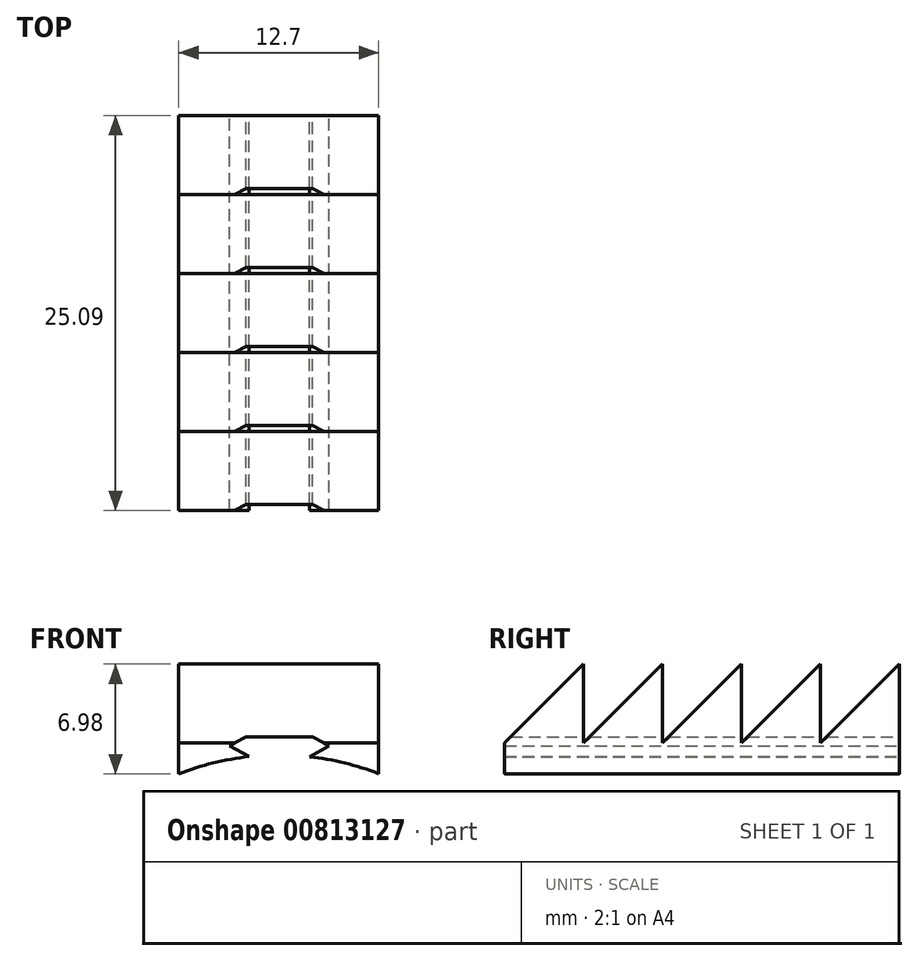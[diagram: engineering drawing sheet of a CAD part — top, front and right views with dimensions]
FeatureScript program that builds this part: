
annotation { "Feature Type Name" : "Feature", "Feature Type Description" : "" }
export const myFeature = defineFeature(function(context is Context, id is Id, definition is map)
    precondition{}
    {
        {
            var Q0;
            Q0=qCreatedBy(makeId("Right.planeOp"),FACE);
            var sketch = newSketch(context, id + "F0", { "sketchPlane" : qUnion([Q0])});
            skLineSegment(sketch, "E0", {"start": v(-27.03, 25.32) * mm, "end": v(-27.03, 20.3) * mm});
            skLineSegment(sketch, "E1", {"start": v(-27.03, 20.3) * mm, "end": v(-22.02, 25.32) * mm});
            skLineSegment(sketch, "E2", {"start": v(-22.02, 25.32) * mm, "end": v(-22.02, 20.3) * mm});
            skLineSegment(sketch, "E3", {"start": v(-27.03, 25.32) * mm, "end": v(-32.05, 20.3) * mm});
            skPoint(sketch, "E4.start.orphan", {"position": v(-5.28, 10.5) * mm});
            skPoint(sketch, "E5.start.orphan", {"position": v(-1.95, 20.3) * mm});
            skPoint(sketch, "E6.orphan", {"position": v(-0.63, 28.3) * mm});
            skPoint(sketch, "E7.right.end.orphan", {"position": v(0, 12.3) * mm});
            skPoint(sketch, "E8.orphan", {"position": v(-0.31, 20.3) * mm});
            skPoint(sketch, "E9.orphan", {"position": v(2.77, 47.92) * mm});
            skPoint(sketch, "E10.orphan", {"position": v(-9.93, -7.31) * mm});
            skPoint(sketch, "E11.orphan", {"position": v(-3.58, 20.3) * mm});
            skLineSegment(sketch, "E12", {"start": v(-22.02, 20.3) * mm, "end": v(-17, 25.32) * mm});
            skLineSegment(sketch, "E13", {"start": v(-17, 25.32) * mm, "end": v(-17, 20.3) * mm});
            skLineSegment(sketch, "E14", {"start": v(-17, 20.3) * mm, "end": v(-17, 25.32) * mm});
            skPoint(sketch, "E14.endSnap0", {"position": v(-17, 20.3) * mm});
            skLineSegment(sketch, "E15", {"start": v(-11.98, 25.32) * mm, "end": v(-17, 20.3) * mm});
            skLineSegment(sketch, "E16", {"start": v(-11.98, 20.3) * mm, "end": v(-11.98, 25.32) * mm});
            skLineSegment(sketch, "E17", {"start": v(-11.98, 20.3) * mm, "end": v(-6.96, 25.32) * mm});
            skLineSegment(sketch, "E18", {"start": v(-6.96, 25.32) * mm, "end": v(-6.96, 20.3) * mm});
            skPoint(sketch, "E19.1.0.0", {"position": v(20.12, 10.5) * mm});
            skPoint(sketch, "E19.2.0.0", {"position": v(45.52, 10.5) * mm});
            skLineSegment(sketch, "E19.direction1", {"start": v(-5.28, 10.5) * mm, "end": v(20.12, 10.5) * mm, "construction": true});
            skLineSegment(sketch, "E20.top", {"start": v(-6.96, 16.73) * mm, "end": v(-32.05, 16.73) * mm});
            skLineSegment(sketch, "E20.left", {"start": v(-6.96, 20.3) * mm, "end": v(-6.96, 16.73) * mm});
            skLineSegment(sketch, "E21", {"start": v(-32.05, 16.73) * mm, "end": v(-32.05, 20.3) * mm});
            skPoint(sketch, "E22.orphan", {"position": v(-31.96, 16.73) * mm});
            skSolve(sketch);
        }
        {
            var Q0;
            Q0=makeQuery(id+"F0.imprint","IMPRINT",FACE,{"disambiguationData":[TD([[makeQuery(id+"F0.imprint","IMPRINT",EDGE,{"derivedFrom":sQuery(id+"F0.wireOp",EDGE,"E0")}),-1.0]])]});
            extrude(context, id + "F1", {"entities" : qUnion([Q0]), "depth" : 12.7 * mm, "offsetDistance" : 25.4 * mm});
        }
        {
            var Q0;
            Q0=makeQuery(id+"F1.opExtrude","CAP_VERTEX",VERTEX,{"disambiguationData":[OSD([sQuery(id+"F0.wireOp",EDGE,"E17"),sQuery(id+"F0.wireOp",EDGE,"E18")])],"isStart":false});
            var Q1;
            Q1=qCreatedBy(makeId("Front.planeOp"),FACE);
            cPlane(context, id + "F2", {"entities" : qUnion([Q0, Q1]), "cplaneType" : CPlaneType.PLANE_POINT, "offset" : 25.4 * mm, "width" : 152.4 * mm, "height" : 152.4 * mm});
        }
        {
            var Q0;
            Q0=qCreatedBy(id+"F2.planeOp",FACE);
            var sketch = newSketch(context, id + "F3", { "sketchPlane" : qUnion([Q0])});
            skCircle(sketch, "E23", {"center": v(6.37, 2.08) * mm, "radius": 17.46 * mm});
            skSolve(sketch);
        }
        {
            var Q0;
            Q0 = qSketchRegion(id + "F3", true);
            extrude(context, id + "F4", {"entities" : qUnion([Q0]), "operationType" : NewBodyOperationType.REMOVE, "depth" : 25.4 * mm, "offsetDistance" : 25.4 * mm});
        }
        {
            var Q0;
            Q0=makeQuery(id+"F1.opExtrude","SWEPT_BODY",BODY,{"disambiguationData":[OSD([sQuery(id+"F0.wireOp",EDGE,"E0"),sQuery(id+"F0.wireOp",EDGE,"E1"),sQuery(id+"F0.wireOp",EDGE,"E2"),sQuery(id+"F0.wireOp",EDGE,"E3"),sQuery(id+"F0.wireOp",EDGE,"E12"),sQuery(id+"F0.wireOp",EDGE,"E13"),sQuery(id+"F0.wireOp",EDGE,"E15"),sQuery(id+"F0.wireOp",EDGE,"E16"),sQuery(id+"F0.wireOp",EDGE,"E17"),sQuery(id+"F0.wireOp",EDGE,"E18"),sQuery(id+"F0.wireOp",EDGE,"E20.top"),sQuery(id+"F0.wireOp",EDGE,"E20.left"),sQuery(id+"F0.wireOp",EDGE,"E20.right"),sQuery(id+"F0.wireOp",EDGE,"0172e36d-b3d0-40e5-9f1f-b767e8603321.trimOffspring")])]});
            transform(context, id + "F5", {"entities" : qUnion([Q0]), "transformType" : TransformType.COPY});
        }
        {
            var Q0;
            Q0=makeQuery(id+"F1.opExtrude","SWEPT_BODY",BODY,{"disambiguationData":[OSD([sQuery(id+"F0.wireOp",EDGE,"E0"),sQuery(id+"F0.wireOp",EDGE,"E1"),sQuery(id+"F0.wireOp",EDGE,"E2"),sQuery(id+"F0.wireOp",EDGE,"E3"),sQuery(id+"F0.wireOp",EDGE,"E12"),sQuery(id+"F0.wireOp",EDGE,"E13"),sQuery(id+"F0.wireOp",EDGE,"E15"),sQuery(id+"F0.wireOp",EDGE,"E16"),sQuery(id+"F0.wireOp",EDGE,"E17"),sQuery(id+"F0.wireOp",EDGE,"E18"),sQuery(id+"F0.wireOp",EDGE,"E20.top"),sQuery(id+"F0.wireOp",EDGE,"E20.left"),sQuery(id+"F0.wireOp",EDGE,"E20.right"),sQuery(id+"F0.wireOp",EDGE,"0172e36d-b3d0-40e5-9f1f-b767e8603321.trimOffspring")])]});
            transform(context, id + "F6", {"entities" : qUnion([Q0]), "transformType" : TransformType.TRANSLATION_3D, "dx" : 0 * mm, "dy" : 26.14 * mm, "dz" : 0 * mm, "makeCopy" : false});
        }
        {
            var Q0;
            Q0=makeQuery(id+"F5.opPattern","COPY",BODY,{"derivedFrom":makeQuery(id+"F1.opExtrude","SWEPT_BODY",BODY,{"disambiguationData":[OSD([sQuery(id+"F0.wireOp",EDGE,"E0"),sQuery(id+"F0.wireOp",EDGE,"E1"),sQuery(id+"F0.wireOp",EDGE,"E2"),sQuery(id+"F0.wireOp",EDGE,"E3"),sQuery(id+"F0.wireOp",EDGE,"E12"),sQuery(id+"F0.wireOp",EDGE,"E13"),sQuery(id+"F0.wireOp",EDGE,"E15"),sQuery(id+"F0.wireOp",EDGE,"E16"),sQuery(id+"F0.wireOp",EDGE,"E17"),sQuery(id+"F0.wireOp",EDGE,"E18"),sQuery(id+"F0.wireOp",EDGE,"E20.top"),sQuery(id+"F0.wireOp",EDGE,"E20.left"),sQuery(id+"F0.wireOp",EDGE,"E20.right"),sQuery(id+"F0.wireOp",EDGE,"0172e36d-b3d0-40e5-9f1f-b767e8603321.trimOffspring")])]}),"instanceName":"1"});
            var Q1;
            Q1=makeQuery(id+"F1.opExtrude","SWEPT_BODY",BODY,{"disambiguationData":[OSD([sQuery(id+"F0.wireOp",EDGE,"E0"),sQuery(id+"F0.wireOp",EDGE,"E1"),sQuery(id+"F0.wireOp",EDGE,"E2"),sQuery(id+"F0.wireOp",EDGE,"E3"),sQuery(id+"F0.wireOp",EDGE,"E12"),sQuery(id+"F0.wireOp",EDGE,"E13"),sQuery(id+"F0.wireOp",EDGE,"E15"),sQuery(id+"F0.wireOp",EDGE,"E16"),sQuery(id+"F0.wireOp",EDGE,"E17"),sQuery(id+"F0.wireOp",EDGE,"E18"),sQuery(id+"F0.wireOp",EDGE,"E20.top"),sQuery(id+"F0.wireOp",EDGE,"E20.left"),sQuery(id+"F0.wireOp",EDGE,"E20.right"),sQuery(id+"F0.wireOp",EDGE,"0172e36d-b3d0-40e5-9f1f-b767e8603321.trimOffspring")])]});
            transform(context, id + "F7", {"entities" : qUnion([Q0, Q1]), "transformType" : TransformType.TRANSLATION_3D, "dx" : 0 * mm, "dy" : 0 * mm, "dz" : 0 * mm, "makeCopy" : false});
        }
        {
            var Q0;
            Q0=makeQuery(id+"F1.opExtrude","SWEPT_BODY",BODY,{"disambiguationData":[OSD([sQuery(id+"F0.wireOp",EDGE,"E0"),sQuery(id+"F0.wireOp",EDGE,"E1"),sQuery(id+"F0.wireOp",EDGE,"E2"),sQuery(id+"F0.wireOp",EDGE,"E3"),sQuery(id+"F0.wireOp",EDGE,"E12"),sQuery(id+"F0.wireOp",EDGE,"E13"),sQuery(id+"F0.wireOp",EDGE,"E15"),sQuery(id+"F0.wireOp",EDGE,"E16"),sQuery(id+"F0.wireOp",EDGE,"E17"),sQuery(id+"F0.wireOp",EDGE,"E18"),sQuery(id+"F0.wireOp",EDGE,"E20.top"),sQuery(id+"F0.wireOp",EDGE,"E20.left"),sQuery(id+"F0.wireOp",EDGE,"E20.right"),sQuery(id+"F0.wireOp",EDGE,"0172e36d-b3d0-40e5-9f1f-b767e8603321.trimOffspring")])]});
            deleteBodies(context, id + "F8", {"entities" : qUnion([Q0])});
        }
        {
            var Q0;
            Q0=qCreatedBy(makeId("Right.planeOp"),FACE);
            var sketch = newSketch(context, id + "F9", { "sketchPlane" : qUnion([Q0])});
            skSolve(sketch);
        }
        {
            var Q0;
            Q0=qCreatedBy(id+"F2.planeOp",FACE);
            var sketch = newSketch(context, id + "F10", { "sketchPlane" : qUnion([Q0])});
            skPoint(sketch, "E24.0.midPoint", {"position": v(6.37, 14.3) * mm});
            skPoint(sketch, "E25.orphan", {"position": v(3.13, 14.3) * mm});
            skPoint(sketch, "E24.0.start.orphan", {"position": v(9.61, 14.3) * mm});
            skPoint(sketch, "E24.cCircle.center.orphan", {"position": v(6.37, 16.17) * mm});
            skPoint(sketch, "E26.middle", {"position": v(6.39, 21.85) * mm});
            skLineSegment(sketch, "E27", {"start": v(9.55, 20.12) * mm, "end": v(8.5, 20.7) * mm});
            skLineSegment(sketch, "E28", {"start": v(3.22, 20.12) * mm, "end": v(6.39, 18.39) * mm});
            skLineSegment(sketch, "E29", {"start": v(9.55, 20.12) * mm, "end": v(6.39, 18.39) * mm});
            skPoint(sketch, "E30.orphan", {"position": v(12.72, 21.85) * mm});
            skPoint(sketch, "E31.orphan", {"position": v(12.72, 25.32) * mm});
            skPoint(sketch, "E32.end.orphan", {"position": v(0.06, 21.85) * mm});
            skPoint(sketch, "E26.top.end.orphan", {"position": v(6.39, 25.32) * mm});
            skPoint(sketch, "E26.left.end.orphan", {"position": v(0.06, 25.32) * mm});
            skPoint(sketch, "E33.orphan", {"position": v(12.72, 18.39) * mm});
            skPoint(sketch, "E26.bottom.start.orphan", {"position": v(0.06, 18.39) * mm});
            skPoint(sketch, "E34.orphan", {"position": v(7.97, 19.25) * mm});
            skPoint(sketch, "E35.start.orphan", {"position": v(6.39, 20.12) * mm});
            skPoint(sketch, "E36.start.orphan", {"position": v(4.8, 19.25) * mm});
            skLineSegment(sketch, "E37", {"start": v(6.39, 20.99) * mm, "end": v(6.39, 20.99) * mm});
            skLineSegment(sketch, "E38", {"start": v(5.33, 20.7) * mm, "end": v(7.44, 20.7) * mm});
            skLineSegment(sketch, "E39", {"start": v(7.44, 20.7) * mm, "end": v(8.5, 20.7) * mm});
            skLineSegment(sketch, "E40", {"start": v(8.5, 20.7) * mm, "end": v(4.28, 20.7) * mm});
            skPoint(sketch, "E41.orphan", {"position": v(4.8, 20.99) * mm});
            skPoint(sketch, "E42.end.orphan", {"position": v(7.97, 20.99) * mm});
            skLineSegment(sketch, "E43", {"start": v(4.28, 20.7) * mm, "end": v(3.22, 20.12) * mm});
            skSolve(sketch);
        }
        {
            var Q0;
            {var subQ1=sQuery(id+"F10.wireOp",EDGE,"E27");Q0=makeQuery(id+"F10.imprint","IMPRINT",FACE,{"disambiguationData":[TD([[makeQuery(id+"F10.imprint","IMPRINT",EDGE,{"derivedFrom":subQ1}),1.0]])]});}
            extrude(context, id + "F11", {"entities" : qUnion([Q0]), "operationType" : NewBodyOperationType.REMOVE, "depth" : 25.4 * mm, "offsetDistance" : 25.4 * mm});
        }
    });
